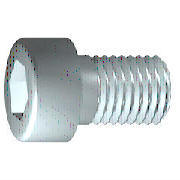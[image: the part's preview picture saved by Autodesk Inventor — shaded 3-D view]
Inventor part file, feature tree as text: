
AUTODESK INVENTOR PART (.ipt)
format: ipt  version: 2018 (Build 220112000, 112)  size: 184,832 bytes
history: native  units: mm (DEFAULTED — no unit token found)
features: sketch x2, extrude x1, plane x1, fillet x1
ambient origin geometry x7: Origin, YZ Plane, XY Plane, X Axis, Y Axis, Z Axis, Center Point
bodies: Solid1 (feature_tree), Body (feature_tree)
feature tree (5):
  extrude  "Slot"  Depth=2.0mm
  plane  "Work Plane1"
  fillet  "Fillet2"  Radius=2.0mm
  sketch  "Sketch1"  dims[d1=19.0mm d2=0.24548mm d3=2.0mm]
  sketch  "Sketch2"  dims[d4=1.0mm d5=60.0deg d6=2.0mm d7=2.0mm d8=1.732051mm d9=3.8mm d10=90.0deg d11=10.0mm d12=0.0mm d13=19.0mm d14=0.0mm d15=0.24538mm d16=0.24538mm d17=0.2mm d19=0.0mm d26=20.0mm d27=45.0deg d28=0.0mm d29=0.0mm d30=0.1mm]
